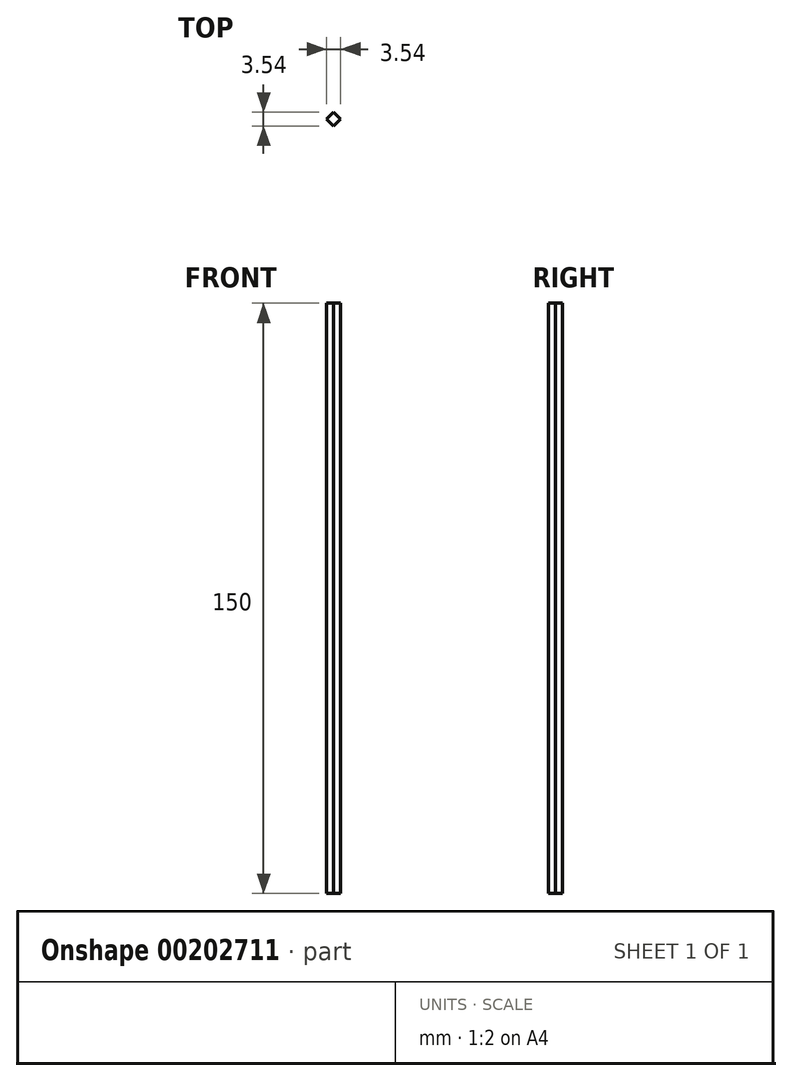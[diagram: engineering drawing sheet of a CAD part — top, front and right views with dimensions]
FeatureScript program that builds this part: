
annotation { "Feature Type Name" : "Feature", "Feature Type Description" : "" }
export const myFeature = defineFeature(function(context is Context, id is Id, definition is map)
    precondition{}
    {
        {
            var Q0;
            Q0=qCreatedBy(makeId("Top.planeOp"),FACE);
            var sketch = newSketch(context, id + "F0", { "sketchPlane" : qUnion([Q0])});
            skLineSegment(sketch, "E0", {"start": v(-0.88, 0.88) * mm, "end": v(0, 1.77) * mm});
            skLineSegment(sketch, "E1", {"start": v(0, 1.77) * mm, "end": v(1.77, 0) * mm});
            skLineSegment(sketch, "E2", {"start": v(1.77, 0) * mm, "end": v(0, -1.77) * mm});
            skLineSegment(sketch, "E3", {"start": v(0, -1.77) * mm, "end": v(-1.77, 0) * mm});
            skLineSegment(sketch, "E4", {"start": v(-1.77, 0) * mm, "end": v(-0.88, 0.88) * mm});
            skSolve(sketch);
        }
        {
            var Q0;
            Q0=makeQuery(id+"F0.imprint","IMPRINT",FACE,{"disambiguationData":[TD([[makeQuery(id+"F0.imprint","IMPRINT",EDGE,{"derivedFrom":sQuery(id+"F0.wireOp",EDGE,"E0")}),-1.0]])]});
            extrude(context, id + "F1", {"entities" : qUnion([Q0]), "depth" : 150 * mm});
        }
    });
